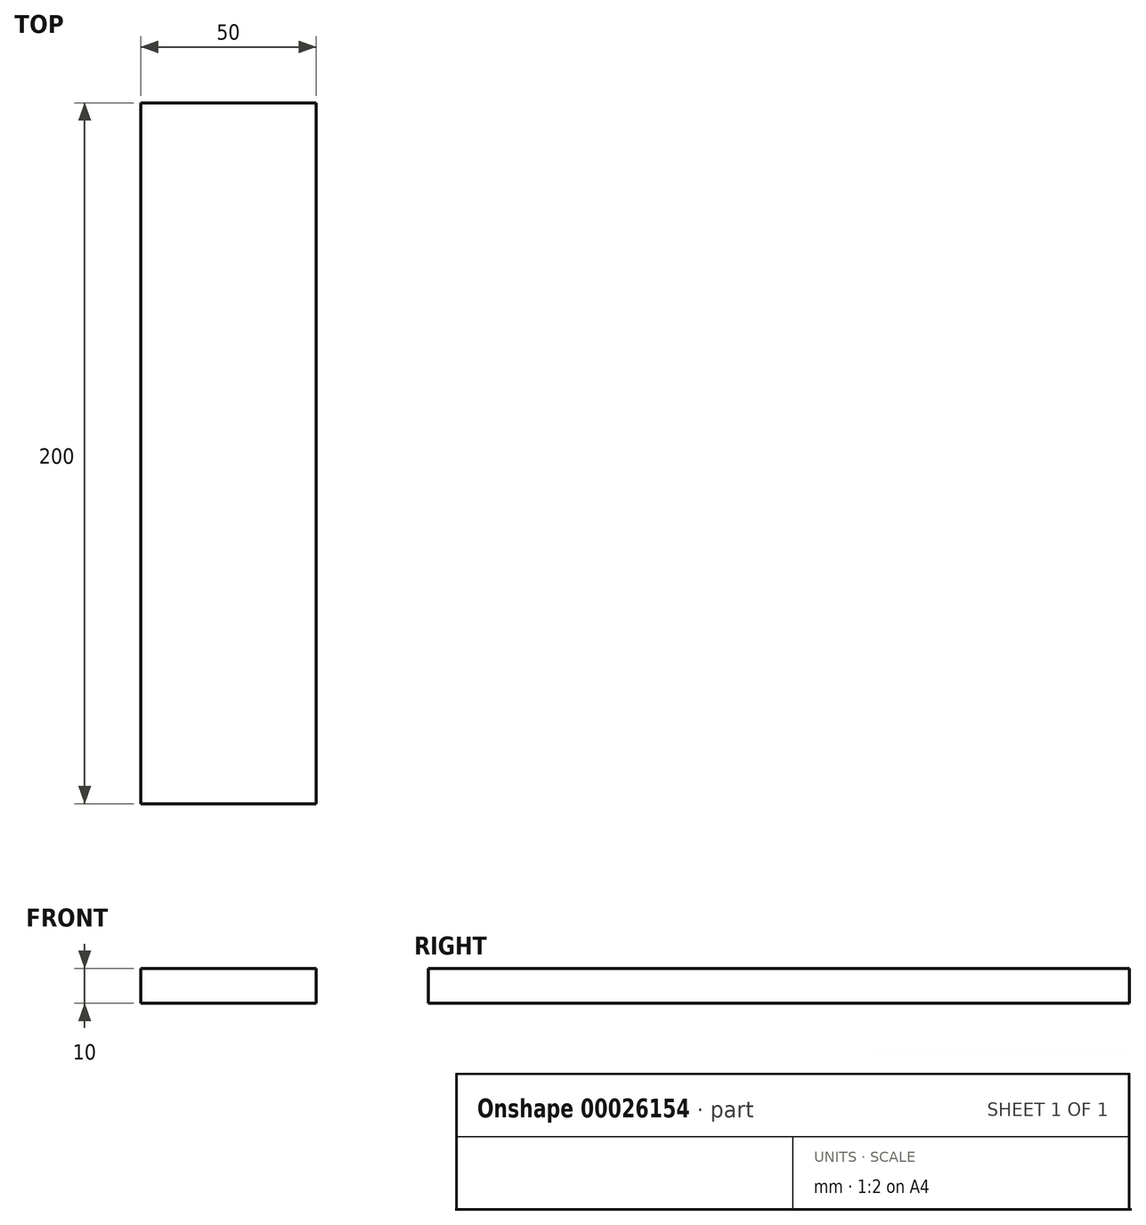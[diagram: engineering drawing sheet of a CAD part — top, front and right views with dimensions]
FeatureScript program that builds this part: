
annotation { "Feature Type Name" : "Feature", "Feature Type Description" : "" }
export const myFeature = defineFeature(function(context is Context, id is Id, definition is map)
    precondition{}
    {
        {
            var Q0;
            Q0=qCreatedBy(makeId("Top.planeOp"),FACE);
            var sketch = newSketch(context, id + "F0", { "sketchPlane" : qUnion([Q0])});
            skLineSegment(sketch, "E0.rect.bottom", {"start": v(-25, -100) * mm, "end": v(25, -100) * mm});
            skLineSegment(sketch, "E0.rect.top", {"start": v(-25, 100) * mm, "end": v(25, 100) * mm});
            skLineSegment(sketch, "E0.rect.left", {"start": v(-25, -100) * mm, "end": v(-25, 100) * mm});
            skLineSegment(sketch, "E0.rect.right", {"start": v(25, -100) * mm, "end": v(25, 100) * mm});
            skPoint(sketch, "E0.rect.middle", {"position": v(0, 0) * mm});
            skSolve(sketch);
        }
        {
            var Q0;
            Q0=makeQuery(id+"F0.imprint","IMPRINT",FACE,{"disambiguationData":[TD([[makeQuery(id+"F0.imprint","IMPRINT",EDGE,{"derivedFrom":sQuery(id+"F0.wireOp",EDGE,"E0.rect.bottom")}),1.0]])]});
            extrude(context, id + "F1", {"entities" : qUnion([Q0]), "depth" : 10 * mm});
        }
    });
